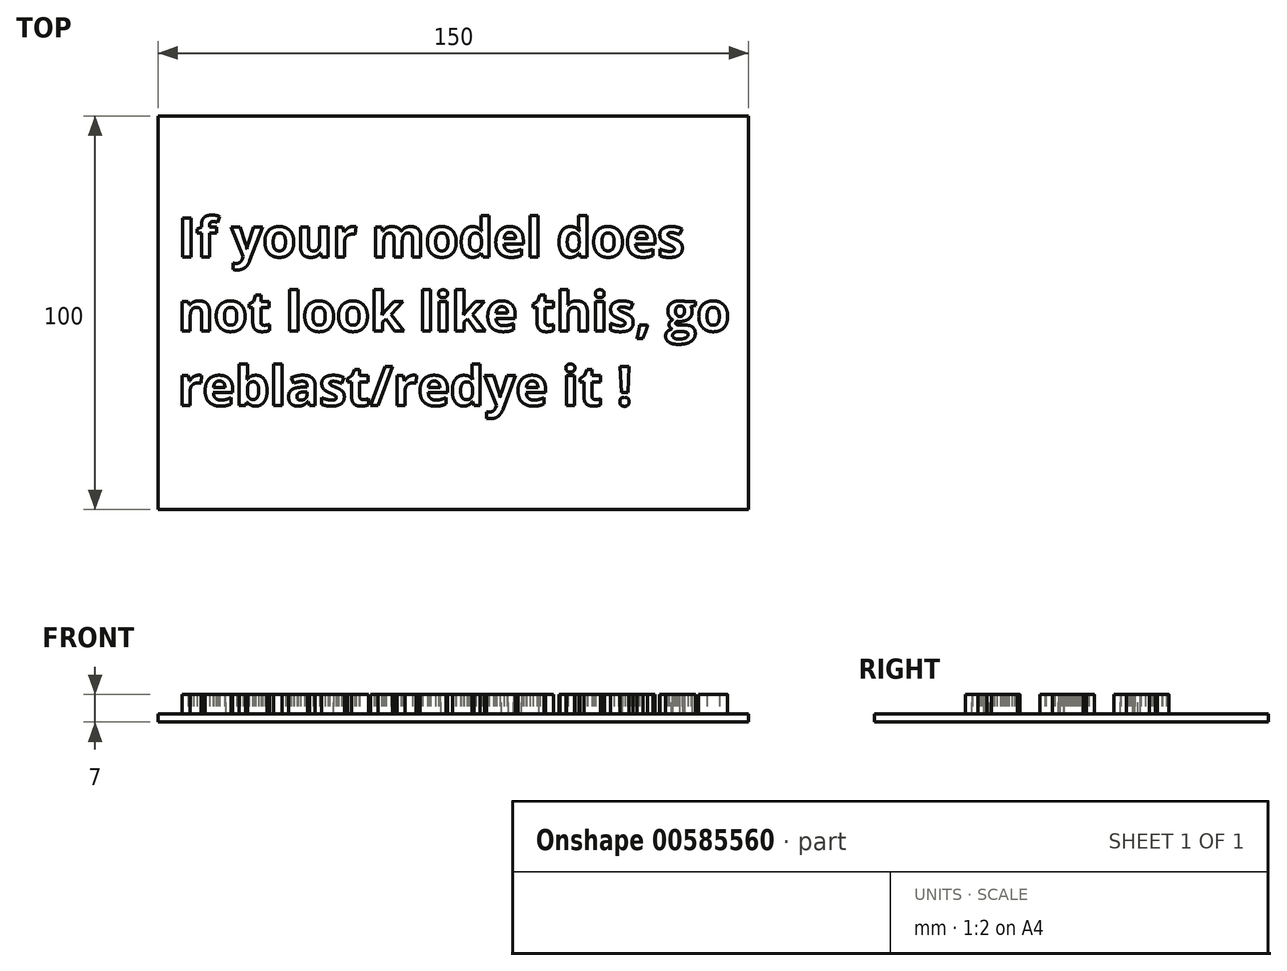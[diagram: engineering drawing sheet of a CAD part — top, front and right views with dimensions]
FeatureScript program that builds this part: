
annotation { "Feature Type Name" : "Feature", "Feature Type Description" : "" }
export const myFeature = defineFeature(function(context is Context, id is Id, definition is map)
    precondition{}
    {
        {
            var Q0;
            Q0=qCreatedBy(makeId("Top.planeOp"),FACE);
            var sketch = newSketch(context, id + "F0", { "sketchPlane" : qUnion([Q0])});
            skLineSegment(sketch, "E0.bottom", {"start": v(75, 50) * mm, "end": v(-75, 50) * mm});
            skLineSegment(sketch, "E0.top", {"start": v(75, -50) * mm, "end": v(-75, -50) * mm});
            skLineSegment(sketch, "E0.left", {"start": v(75, 50) * mm, "end": v(75, -50) * mm});
            skLineSegment(sketch, "E0.right", {"start": v(-75, 50) * mm, "end": v(-75, -50) * mm});
            skPoint(sketch, "E0.middle", {"position": v(0, 0) * mm});
            skSolve(sketch);
        }
        {
            var Q0;
            Q0=qCreatedBy(makeId("Top.planeOp"),FACE);
            var sketch = newSketch(context, id + "F1", { "sketchPlane" : qUnion([Q0])});
            skText(sketch, "E1", { "text": "If your model does \nnot look like this, go \nreblast/redye it !", "fontName": "OpenSans-Bold.ttf"});
            const initialGuessF1  = {"E1": [-0.07001, 0.01417, 1, 0, 0.01]};
            skSetInitialGuess(sketch, initialGuessF1);
            skSolve(sketch);
        }
        {
            var Q0;
            Q0=makeQuery(id+"F0.imprint","IMPRINT",FACE,{"disambiguationData":[TD([[makeQuery(id+"F0.imprint","IMPRINT",EDGE,{"derivedFrom":sQuery(id+"F0.wireOp",EDGE,"E0.bottom")}),1.0]])]});
            extrude(context, id + "F2", {"entities" : qUnion([Q0]), "oppositeDirection" : true, "depth" : 2 * mm, "offsetDistance" : 25 * mm});
        }
        {
            var Q0;
            Q0 = qSketchRegion(id + "F1", true);
            extrude(context, id + "F3", {"entities" : qUnion([Q0]), "operationType" : NewBodyOperationType.ADD, "depth" : 5 * mm, "offsetDistance" : 25 * mm});
        }
    });
